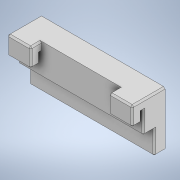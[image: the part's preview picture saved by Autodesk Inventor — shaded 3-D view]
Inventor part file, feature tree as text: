
AUTODESK INVENTOR PART (.ipt)
format: ipt  version: 2020 (Build 240168000, 168)  size: 195,584 bytes
history: native  units: mm
features: extrude x7, sketch x7, chamfer x1
ambient origin geometry x8: Origin, YZ Plane, XZ Plane, XY Plane, X Axis, Y Axis, Z Axis, Center Point
bodies: Solid1 (feature_tree)
feature tree (15):
  extrude  "Extrusion1"  Depth=20.0mm
  extrude  "Extrusion2"  Depth=80.0mm
  extrude  "Extrusion3"  Depth=7.0mm TaperAngle=0.0deg
  extrude  "Extrusion6"  Depth=5.0mm
  extrude  "Extrusion7"  Depth=50.0mm
  extrude  "Extrusion8"  Depth=7.0mm TaperAngle=0.0deg
  extrude  "Extrusion9"  Depth=35.0mm
  chamfer  "Chamfer5"  Distance=7.0mm
  sketch  "Sketch1"  dims[d0=80.0mm d1=20.0mm]
  sketch  "Sketch2"  dims[d2=7.0mm d3=0.0mm d4=80.0mm]
  sketch  "Sketch3"  dims[d5=5.0mm d6=7.0mm d7=0.0mm]
  sketch  "Sketch6"  dims[d8=80.0mm d9=5.0mm]
  sketch  "Sketch7"  dims[d10=7.0mm d11=0.0mm d28=50.0mm]
  sketch  "Sketch8"  dims[d29=15.0mm d30=7.0mm d31=0.0mm]
  sketch  "Sketch9"  dims[d38=80.0mm d39=35.0mm d40=7.0mm d41=0.0mm d42=5.0mm d43=17.75mm d44=20.0mm d45=5.0mm d46=0.0mm d47=5.0mm d48=17.75mm d49=20.0mm d50=5.0mm d51=0.0mm d52=1.0mm d53=2.0mm d54=45.0deg]
